# Revit family: Domotics-DomesticRanges-GEWISS-CHORUS_SIGNALLING-LAMP_SPORGENTI_2M
name_source: partatom
category: Apparecchi elettrici
revit_build: Autodesk Revit 2016 (Build: 20161004_0715(x64)
units: mm (PartAtom-declared; Revit-internal decimal feet)

## family parameters
Condiviso = Sì
Host = Superficie
Mantenere orientamento annotazione = Sì
Punto di calcolo locali = Sì
Quota connettore circolare = Usa diametro
Taglio con vuoti quando caricato = Sì
Tipo di parte = Normale

## types (12) — shared parameters
Catalogue = DOMOTICS
Catalogue Range = CHORUS - DOMESTIC RANGE
Description. = Protruding indicator lamp
Electrocod = 0132
IDF = 8d5fe462-2424-4b85-a35d-1cd6d5551717
IDT = e0227ad7-94cc-48c5-9b66-293781f40d4f
Immagine tipo = GW14634.jpg
Lamp = LED
No. Chorus modules = 2
No. Chorus modules: = 2
Produttore = GEWISS S.p.A.
Prospetto di default = 1219 mm
SEO = Indicator
Supply voltage = 12V ac/dc - 230V ac 50/60 Hz
Technical sheet = https://www.gewiss.com
Tipo = Chorus Spie Sporgenti 2M_GENERICO : GW14634 Spia sporgente ambra 3W 2M titanio
Type of lamp = LED
URL = https://www.gewiss.com
Version file RFA = 19.0

## per-type parameters (varying)
| type | Colour | Descrizione | Diffuser colour | EAN code | Modello |
| GW12633 - Red protruding indicator lamp 3W 2M black | Black | RED PROTRUDING INDICATOR LAMP 3W 2M B | Red | 8011564269316 | GW12633 |
| GW12634 - Amber protruding indicator lamp 3W 2M black | Black | AMBER PROTRUDING INDICATOR LAMP 3W 2M B | Amber | 8011564269323 | GW12634 |
| GW12631 - Transp protruding indicator lamp 3W 2M black | Black | TRANSP PROTRUDING INDICATOR LAMP 3W 2M B | Opal | 8011564269293 | GW12631 |
| GW10632 - Green protruding indicator lamp 3W 2M white | White | GREEN PROTRUDING INDICATOR LAMP 3W 2M W | Green | 8011564259058 | GW10632 |
| GW14633 - Red protruding indicator lamp 3W 2M titanium | Titanium | RED PROTRUDING INDICATOR LAMP 3W 2M T | Red | 8011564268586 | GW14633 |
| GW12632 - Green protruding indicator lamp 3W 2M black | Black | GREEN PROTRUDING INDICATOR LAMP 3W 2M B | Green | 8011564269309 | GW12632 |
| GW10631 - Transp protruding indicator lamp 3W 2M white | White | TRANSP PROTRUDING INDICATOR LAMP 3W 2M W | Opal | 8011564259041 | GW10631 |
| GW10633 - Red protruding indicator lamp 3W 2M white | White | RED PROTRUDING INDICATOR LAMP 3W 2M W | Red | 8011564259065 | GW10633 |
| GW14631 - Transp protruding indicator lamp 3W 2M titanium | Titanium | TRANSP PROTRUDING INDICATOR LAMP 3W 2M T | Opal | 8011564268548 | GW14631 |
| GW14634 - Amber protruding indicator lamp 3W 2M titanium | Titanium | AMBER PROTRUDING INDICATOR LAMP 3W 2M T | Amber | 8011564268593 | GW14634 |
| GW14632 - Green protruding indicator lamp 3W 2M titanium | Titanium | GREEN PROTRUDING INDICATOR LAMP 3W 2M T | Green | 8011564268555 | GW14632 |
| GW10634 - Amber protruding indicator lamp 3W 2M white | White | AMBER PROTRUDING INDICATOR LAMP 3W 2M W | Amber | 8011564259072 | GW10634 |

## geometry (parser evidence)
native form markers: Sweep x2
no freeform markers — native parametric forms only
